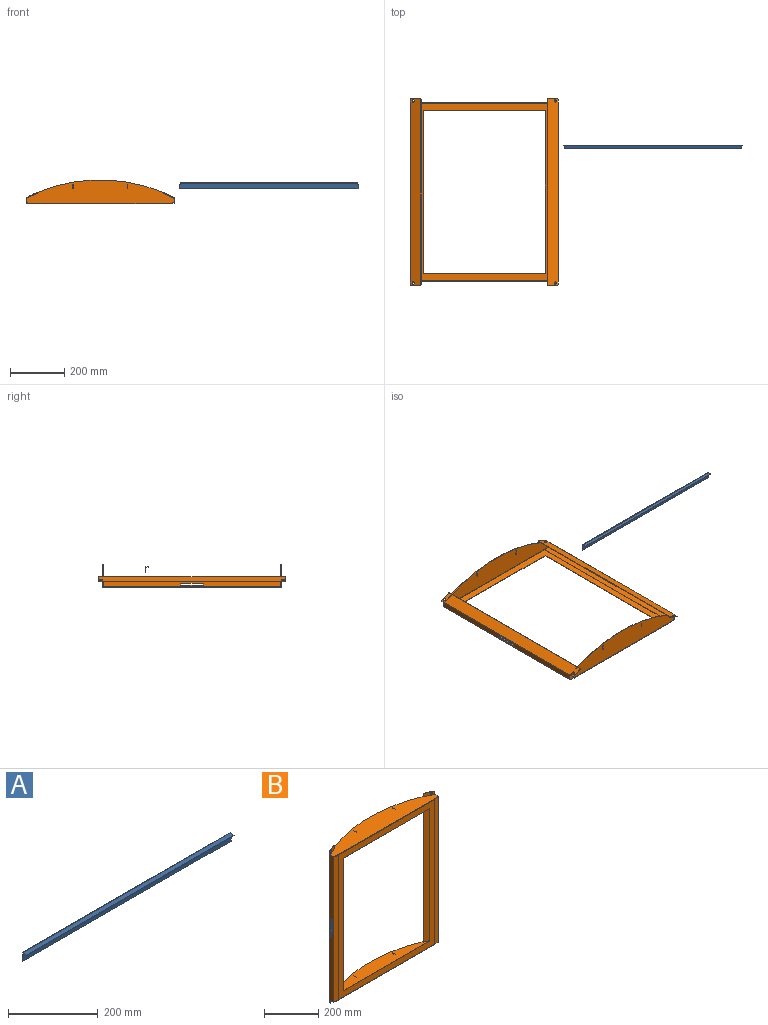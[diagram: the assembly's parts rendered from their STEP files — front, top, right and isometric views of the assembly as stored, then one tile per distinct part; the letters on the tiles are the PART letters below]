
ASSEMBLY  parts=2 mates=1
PART A: 17 faces, bbox 655.5x12.4x24.1 mm
  f0: plane 655.5x22.51mm, normal (0,1,0), area 14729.5mm2, adj f2,f3,f4,f5,f6,f7,f8,f10
  f1: plane 655.5x22.51mm, normal (0,-1,0), area 14729.5mm2, adj f2,f3,f4,f5,f6,f7,f8,f16
  f2: plane 7.51x1.59mm, normal (-1,0,0), area 11.9mm2, adj f0,f1,f7,f9
  f3: plane 7.51x1.59mm, normal (1,0,0), area 11.9mm2, adj f0,f1,f8,f11
  f4: plane 15x1.59mm, normal (1,0,0), area 23.8mm2, adj f0,f1,f5,f8
  f5: plane 655.5x1.59mm, normal (0,0,-1), area 1040.6mm2, adj f0,f1,f4,f6
  f6: plane 15x1.59mm, normal (-1,0,0), area 23.8mm2, adj f0,f1,f5,f7
  f7: plane 1.59x1.59mm, normal (0,0,1), area 2.5mm2, adj f0,f1,f2,f6
  f8: plane 1.59x1.59mm, normal (0,0,1), area 2.5mm2, adj f0,f1,f3,f4
  f9: plane 1.92x1.59mm, normal (-1,0,0), area 2.2mm2, adj f2,f10,f13
  f10: cylinder r=1.59mm len=652.33mm, axis (1,0,0), area 1843.6mm2, adj f0,f9,f11,f15
  f11: plane 1.92x1.59mm, normal (1,0,0), area 2.2mm2, adj f3,f10,f12
  f12: plane 10.84x3.79mm, normal (1,0,0), area 17mm2, adj f11,f14,f15,f16
  f13: plane 10.84x3.79mm, normal (-1,0,0), area 17mm2, adj f9,f14,f15,f16
  f14: plane 652.33x1.55mm, normal (0,-0.98,-0.21), area 1035.6mm2, adj f12,f13,f15,f16
  f15: plane 652.33x10.51mm, normal (0,-0.21,0.98), area 7005.7mm2, adj f10,f12,f13,f14
  f16: plane 652.33x10.51mm, normal (0,0.21,-0.98), area 7005.7mm2, adj f1,f12,f13,f14
PART B: 142 faces, bbox 546.1x88.6x685 mm
  f0: plane 1.83x1.81mm, normal (0,0,1), area 2.2mm2, adj f4,f23,f47,f125
  f1: plane 1.83x1.81mm, normal (0,0,-1), area 2.2mm2, adj f2,f23,f47,f122
  f2: plane 17.09x1.61mm, normal (0,0,-1), area 27.6mm2, adj f1,f5,f24,f46
  f3: plane 1.97x1.94mm, normal (0,0,1), area 2.7mm2, adj f4,f8,f25,f45
  f4: plane 17.09x1.61mm, normal (0,0,1), area 27.6mm2, adj f0,f3,f24,f46
  f5: plane 1.97x1.94mm, normal (0,0,-1), area 2.7mm2, adj f2,f6,f25,f45
  f6: plane 21.42x4.56mm, normal (0,0,-1), area 34.5mm2, adj f5,f9,f26,f44
  f7: plane 1.62x0.28mm, normal (0,0,1), area 0.3mm2, adj f8,f27,f43,f48
  f8: plane 21.42x4.56mm, normal (0,0,1), area 34.5mm2, adj f3,f7,f26,f44
  f9: plane 1.62x0.28mm, normal (0,0,-1), area 0.3mm2, adj f6,f27,f43,f55
  f10: plane 1.62x0.28mm, normal (0,0,1), area 0.3mm2, adj f14,f29,f41,f49
  f11: plane 1.62x0.28mm, normal (0,0,-1), area 0.3mm2, adj f12,f29,f41,f54
  f12: plane 21.42x4.56mm, normal (0,0,-1), area 34.5mm2, adj f11,f15,f30,f40
  f13: plane 1.97x1.94mm, normal (0,0,1), area 2.7mm2, adj f14,f18,f31,f39
  f14: plane 21.42x4.56mm, normal (0,0,1), area 34.5mm2, adj f10,f13,f30,f40
  f15: plane 1.97x1.94mm, normal (0,0,-1), area 2.7mm2, adj f12,f16,f31,f39
  f16: plane 17.09x1.61mm, normal (0,0,-1), area 27.6mm2, adj f15,f19,f32,f38
  f17: plane 1.83x1.81mm, normal (0,0,1), area 2.2mm2, adj f18,f33,f37,f128
  f18: plane 17.09x1.61mm, normal (0,0,1), area 27.6mm2, adj f13,f17,f32,f38
  f19: plane 1.83x1.81mm, normal (0,0,-1), area 2.2mm2, adj f16,f33,f37,f131
  f20: plane 685x39.21mm, normal (0.42,-0.91,0), area 29445.4mm2, adj f21,f47,f122,f123,f124,f125,f126,f127
  f21: plane 678.65x1.46mm, normal (0.91,0.42,0), area 1094.6mm2, adj f20,f22,f138,f140
  f22: plane 685x39.21mm, normal (-0.42,0.91,0), area 29445.4mm2, adj f21,f23,f122,f123,f124,f125,f126,f127
  f23: cylinder r=1.99mm len=651.56mm, axis (0,0,-1), area 1479.5mm2, adj f0,f1,f22,f24
  f24: plane 651.56x17.09mm, normal (-1,0,0), area 10609mm2, adj f2,f4,f23,f25,f114,f115,f116,f117
  f25: cylinder r=1.99mm len=651.56mm, axis (0,0,-1), area 1860.4mm2, adj f3,f5,f24,f26
  f26: plane 651.56x21.2mm, normal (-0.14,-0.99,0), area 13943.9mm2, adj f6,f8,f25,f27
  f27: cylinder r=1.99mm len=651.56mm, axis (0,0,-1), area 180.3mm2, adj f7,f9,f26,f28
  f28: plane 651.56x499.72mm, normal (0,-1,0), area 57790.7mm2, adj f27,f29,f50,f56,f94,f95,f96,f97
  f29: cylinder r=1.99mm len=651.56mm, axis (0,0,-1), area 180.3mm2, adj f10,f11,f28,f30
  f30: plane 651.56x21.2mm, normal (0.14,-0.99,0), area 13943.9mm2, adj f12,f14,f29,f31
  f31: cylinder r=1.99mm len=651.56mm, axis (0,0,-1), area 1860.4mm2, adj f13,f15,f30,f32
  f32: plane 651.56x17.09mm, normal (1,0,0), area 10609mm2, adj f16,f18,f31,f33,f118,f119,f120,f121
  f33: cylinder r=1.99mm len=651.56mm, axis (0,0,-1), area 1479.5mm2, adj f17,f19,f32,f34
  f34: plane 685x39.21mm, normal (0.42,0.91,0), area 29445.4mm2, adj f33,f35,f128,f129,f130,f131,f132,f133
  f35: plane 678.65x1.46mm, normal (-0.91,0.42,0), area 1094.6mm2, adj f34,f36,f135,f136
  f36: plane 685x39.21mm, normal (-0.42,-0.91,0), area 29445.4mm2, adj f35,f37,f128,f129,f130,f131,f132,f133
  f37: cylinder r=0.38mm len=651.56mm, axis (0,0,-1), area 282.7mm2, adj f17,f19,f36,f38
  f38: plane 651.56x17.09mm, normal (-1,0,0), area 10609mm2, adj f16,f18,f37,f39,f118,f119,f120,f121
  f39: cylinder r=0.38mm len=651.56mm, axis (0,0,-1), area 355.5mm2, adj f13,f15,f38,f40
  f40: plane 651.56x21.2mm, normal (-0.14,0.99,0), area 13943.9mm2, adj f12,f14,f39,f41
  f41: cylinder r=0.38mm len=651.56mm, axis (0,0,-1), area 34.4mm2, adj f10,f11,f40,f42
  f42: plane 651.56x499.72mm, normal (0,1,0), area 57790.7mm2, adj f41,f43,f51,f57,f94,f95,f96,f97
  f43: cylinder r=0.38mm len=651.56mm, axis (0,0,-1), area 34.4mm2, adj f7,f9,f42,f44
  f44: plane 651.56x21.2mm, normal (0.14,0.99,0), area 13943.9mm2, adj f6,f8,f43,f45
  f45: cylinder r=0.38mm len=651.56mm, axis (0,0,-1), area 355.5mm2, adj f3,f5,f44,f46
  f46: plane 651.56x17.09mm, normal (1,0,0), area 10609mm2, adj f2,f4,f45,f47,f114,f115,f116,f117
  f47: cylinder r=0.38mm len=651.56mm, axis (0,0,-1), area 282.7mm2, adj f0,f1,f20,f46
  f48: plane 1.99x1.99mm, normal (-1,0,0), area 3mm2, adj f7,f50,f51,f60
  f49: plane 1.99x1.99mm, normal (1,0,0), area 3mm2, adj f10,f50,f51,f76
  f50: cylinder r=1.99mm len=499.72mm, axis (1,0,0), area 1565.1mm2, adj f28,f48,f49,f52
  f51: cylinder r=0.38mm len=499.72mm, axis (1,0,0), area 299.1mm2, adj f42,f48,f49,f53
  f52: plane 546.1x88.44mm, normal (0,0,1), area 35406.5mm2, adj f50,f60,f61,f62,f63,f64,f65,f66
  f53: plane 546.1x88.44mm, normal (0,0,-1), area 35406.5mm2, adj f51,f60,f61,f62,f63,f64,f65,f66
  f54: plane 1.99x1.99mm, normal (1,0,0), area 3mm2, adj f11,f56,f57,f77
  f55: plane 1.99x1.99mm, normal (-1,0,0), area 3mm2, adj f9,f56,f57,f93
  f56: cylinder r=1.99mm len=499.72mm, axis (-1,0,0), area 1565.1mm2, adj f28,f54,f55,f58
  f57: cylinder r=0.38mm len=499.72mm, axis (-1,0,0), area 299.1mm2, adj f42,f54,f55,f59
  f58: plane 546.1x88.44mm, normal (0,0,-1), area 35406.5mm2, adj f56,f77,f78,f79,f80,f81,f82,f83
  f59: plane 546.1x88.44mm, normal (0,0,1), area 35406.5mm2, adj f57,f77,f78,f79,f80,f81,f82,f83
  f60: plane 1.61x1.59mm, normal (0,-1,0), area 2.6mm2, adj f48,f52,f53,f61
  f61: plane 1.79x1.61mm, normal (1,0,0), area 2.9mm2, adj f52,f53,f60,f62
  f62: plane 19.88x2.78mm, normal (-0.14,-0.99,0), area 32.4mm2, adj f52,f53,f61,f63
  f63: cylinder r=1.99mm len=1.97mm, axis (0,0,1), area 4.6mm2, adj f52,f53,f62,f64
  f64: plane 16.74x1.61mm, normal (-1,0,0), area 27mm2, adj f52,f53,f63,f65
  f65: plane 2.15x1.61mm, normal (0,1,0), area 3.5mm2, adj f52,f53,f64,f66
  f66: plane 39.9x18.39mm, normal (-0.42,0.91,0), area 70.9mm2, adj f52,f53,f65,f67
  f67: plane 2.11x1.61mm, normal (-0.91,-0.42,0), area 3.7mm2, adj f52,f53,f66,f68
  f68: cylinder r=602.49mm len=463.94mm, axis (0,0,1), area 768.1mm2, adj f52,f53,f67,f69
  f69: plane 2.11x1.61mm, normal (0.91,-0.42,0), area 3.7mm2, adj f52,f53,f68,f70
  f70: plane 39.9x18.39mm, normal (0.42,0.91,0), area 70.9mm2, adj f52,f53,f69,f71
  f71: plane 2.15x1.61mm, normal (0,1,0), area 3.5mm2, adj f52,f53,f70,f72
  f72: plane 16.74x1.61mm, normal (1,0,0), area 27mm2, adj f52,f53,f71,f73
  f73: cylinder r=1.99mm len=1.97mm, axis (0,0,1), area 4.6mm2, adj f52,f53,f72,f74
  f74: plane 19.88x2.78mm, normal (0.14,-0.99,0), area 32.4mm2, adj f52,f53,f73,f75
  f75: plane 1.79x1.61mm, normal (-1,0,0), area 2.9mm2, adj f52,f53,f74,f76
  f76: plane 1.61x1.59mm, normal (0,-1,0), area 2.6mm2, adj f49,f52,f53,f75
  f77: plane 1.61x1.59mm, normal (0,-1,0), area 2.6mm2, adj f54,f58,f59,f78
  f78: plane 1.79x1.61mm, normal (-1,0,0), area 2.9mm2, adj f58,f59,f77,f79
  f79: plane 19.88x2.78mm, normal (0.14,-0.99,0), area 32.4mm2, adj f58,f59,f78,f80
  f80: cylinder r=1.99mm len=1.97mm, axis (0,0,-1), area 4.6mm2, adj f58,f59,f79,f81
  f81: plane 16.74x1.61mm, normal (1,0,0), area 27mm2, adj f58,f59,f80,f82
  f82: plane 2.15x1.61mm, normal (0,1,0), area 3.5mm2, adj f58,f59,f81,f83
  f83: plane 39.9x18.39mm, normal (0.42,0.91,0), area 70.9mm2, adj f58,f59,f82,f84
  f84: plane 2.11x1.61mm, normal (0.91,-0.42,0), area 3.7mm2, adj f58,f59,f83,f85
  f85: cylinder r=602.49mm len=463.94mm, axis (0,0,-1), area 768.1mm2, adj f58,f59,f84,f86
  f86: plane 2.11x1.61mm, normal (-0.91,-0.42,0), area 3.7mm2, adj f58,f59,f85,f87
  f87: plane 39.9x18.39mm, normal (-0.42,0.91,0), area 70.9mm2, adj f58,f59,f86,f88
  f88: plane 2.15x1.61mm, normal (0,1,0), area 3.5mm2, adj f58,f59,f87,f89
  f89: plane 16.74x1.61mm, normal (-1,0,0), area 27mm2, adj f58,f59,f88,f90
  f90: cylinder r=1.99mm len=1.97mm, axis (0,0,-1), area 4.6mm2, adj f58,f59,f89,f91
  f91: plane 19.88x2.78mm, normal (-0.14,-0.99,0), area 32.4mm2, adj f58,f59,f90,f92
  f92: plane 1.79x1.61mm, normal (1,0,0), area 2.9mm2, adj f58,f59,f91,f93
  f93: plane 1.61x1.59mm, normal (0,-1,0), area 2.6mm2, adj f55,f58,f59,f92
  f94: plane 596.9x1.61mm, normal (-1,0,0), area 962.7mm2, adj f28,f42,f95,f97
  f95: plane 448.67x1.61mm, normal (0,0,-1), area 723.7mm2, adj f28,f42,f94,f96
  f96: plane 596.9x1.61mm, normal (1,0,0), area 962.7mm2, adj f28,f42,f95,f97
  f97: plane 448.67x1.61mm, normal (0,0,1), area 723.7mm2, adj f28,f42,f94,f96
  f98: plane 1.73x1.61mm, normal (0,-1,0), area 2.8mm2, adj f58,f59,f99,f101
  f99: plane 15.14x1.61mm, normal (1,0,0), area 24.4mm2, adj f58,f59,f98,f100
  f100: plane 1.73x1.61mm, normal (0,1,0), area 2.8mm2, adj f58,f59,f99,f101
  f101: plane 15.14x1.61mm, normal (-1,0,0), area 24.4mm2, adj f58,f59,f98,f100
  f102: plane 15.14x1.61mm, normal (-1,0,0), area 24.4mm2, adj f52,f53,f103,f105
  f103: plane 1.73x1.61mm, normal (0,1,0), area 2.8mm2, adj f52,f53,f102,f104
  f104: plane 15.14x1.61mm, normal (1,0,0), area 24.4mm2, adj f52,f53,f103,f105
  f105: plane 1.73x1.61mm, normal (0,-1,0), area 2.8mm2, adj f52,f53,f102,f104
  f106: plane 1.73x1.61mm, normal (0,-1,0), area 2.8mm2, adj f58,f59,f107,f109
  f107: plane 15.14x1.61mm, normal (1,0,0), area 24.4mm2, adj f58,f59,f106,f108
  f108: plane 1.73x1.61mm, normal (0,1,0), area 2.8mm2, adj f58,f59,f107,f109
  f109: plane 15.14x1.61mm, normal (-1,0,0), area 24.4mm2, adj f58,f59,f106,f108
  f110: plane 15.14x1.61mm, normal (-1,0,0), area 24.4mm2, adj f52,f53,f111,f113
  f111: plane 1.73x1.61mm, normal (0,1,0), area 2.8mm2, adj f52,f53,f110,f112
  f112: plane 15.14x1.61mm, normal (1,0,0), area 24.4mm2, adj f52,f53,f111,f113
  f113: plane 1.73x1.61mm, normal (0,-1,0), area 2.8mm2, adj f52,f53,f110,f112
  f114: plane 82.55x1.61mm, normal (0,-1,0), area 133.1mm2, adj f24,f46,f115,f117
  f115: plane 6.35x1.61mm, normal (0,0,-1), area 10.2mm2, adj f24,f46,f114,f116
  f116: plane 82.55x1.61mm, normal (0,1,0), area 133.1mm2, adj f24,f46,f115,f117
  f117: plane 6.35x1.61mm, normal (0,0,1), area 10.2mm2, adj f24,f46,f114,f116
  f118: plane 6.35x1.61mm, normal (0,0,1), area 10.2mm2, adj f32,f38,f119,f121
  f119: plane 82.55x1.61mm, normal (0,1,0), area 133.1mm2, adj f32,f38,f118,f120
  f120: plane 6.35x1.61mm, normal (0,0,-1), area 10.2mm2, adj f32,f38,f119,f121
  f121: plane 82.55x1.61mm, normal (0,-1,0), area 133.1mm2, adj f32,f38,f118,f120
  f122: plane 13.54x1.46mm, normal (-0.91,-0.42,0), area 21.8mm2, adj f1,f20,f22,f139
  f123: plane 34.12x16.88mm, normal (0,0,-1), area 59.4mm2, adj f20,f22,f138,f139
  f124: plane 34.12x16.88mm, normal (0,0,1), area 59.4mm2, adj f20,f22,f140,f141
  f125: plane 13.54x1.46mm, normal (-0.91,-0.42,0), area 21.8mm2, adj f0,f20,f22,f141
  f126: cylinder r=4.37mm len=8.74mm, axis (-0.42,0.91,0), area 44.3mm2, adj f20,f22
  f127: cylinder r=4.37mm len=8.74mm, axis (-0.42,0.91,0), area 44.3mm2, adj f20,f22
  f128: plane 13.54x1.46mm, normal (0.91,-0.42,0), area 21.8mm2, adj f17,f34,f36,f137
  f129: plane 34.12x16.88mm, normal (0,0,1), area 59.4mm2, adj f34,f36,f136,f137
  f130: plane 34.12x16.88mm, normal (0,0,-1), area 59.4mm2, adj f34,f36,f134,f135
  f131: plane 13.54x1.46mm, normal (0.91,-0.42,0), area 21.8mm2, adj f19,f34,f36,f134
  f132: cylinder r=4.37mm len=8.74mm, axis (0.42,0.91,0), area 44.3mm2, adj f34,f36
  f133: cylinder r=4.37mm len=8.74mm, axis (0.42,0.91,0), area 44.3mm2, adj f34,f36
  f134: cylinder r=3.17mm len=3.56mm, axis (0.42,0.91,0), area 8mm2, adj f34,f36,f130,f131
  f135: cylinder r=3.17mm len=3.56mm, axis (0.42,0.91,0), area 8mm2, adj f34,f35,f36,f130
  f136: cylinder r=3.17mm len=3.56mm, axis (0.42,0.91,0), area 8mm2, adj f34,f35,f36,f129
  f137: cylinder r=3.17mm len=3.56mm, axis (0.42,0.91,0), area 8mm2, adj f34,f36,f128,f129
  f138: cylinder r=3.17mm len=3.56mm, axis (-0.42,0.91,0), area 8mm2, adj f20,f21,f22,f123
  f139: cylinder r=3.17mm len=3.56mm, axis (-0.42,0.91,0), area 8mm2, adj f20,f22,f122,f123
  f140: cylinder r=3.17mm len=3.56mm, axis (-0.42,0.91,0), area 8mm2, adj f20,f21,f22,f124
  f141: cylinder r=3.17mm len=3.56mm, axis (-0.42,0.91,0), area 8mm2, adj f20,f22,f124,f125
PLACE A t=(46.22,-570.88,-886.91)mm
PLACE B rot(axis=(1,0,0),90deg) t=(-573.68,-613.62,2.18)mm
MATE planar B.f106 <-> A.f7  axis (0,0,-1) through (-674.54,-286.65,72.47)mm
